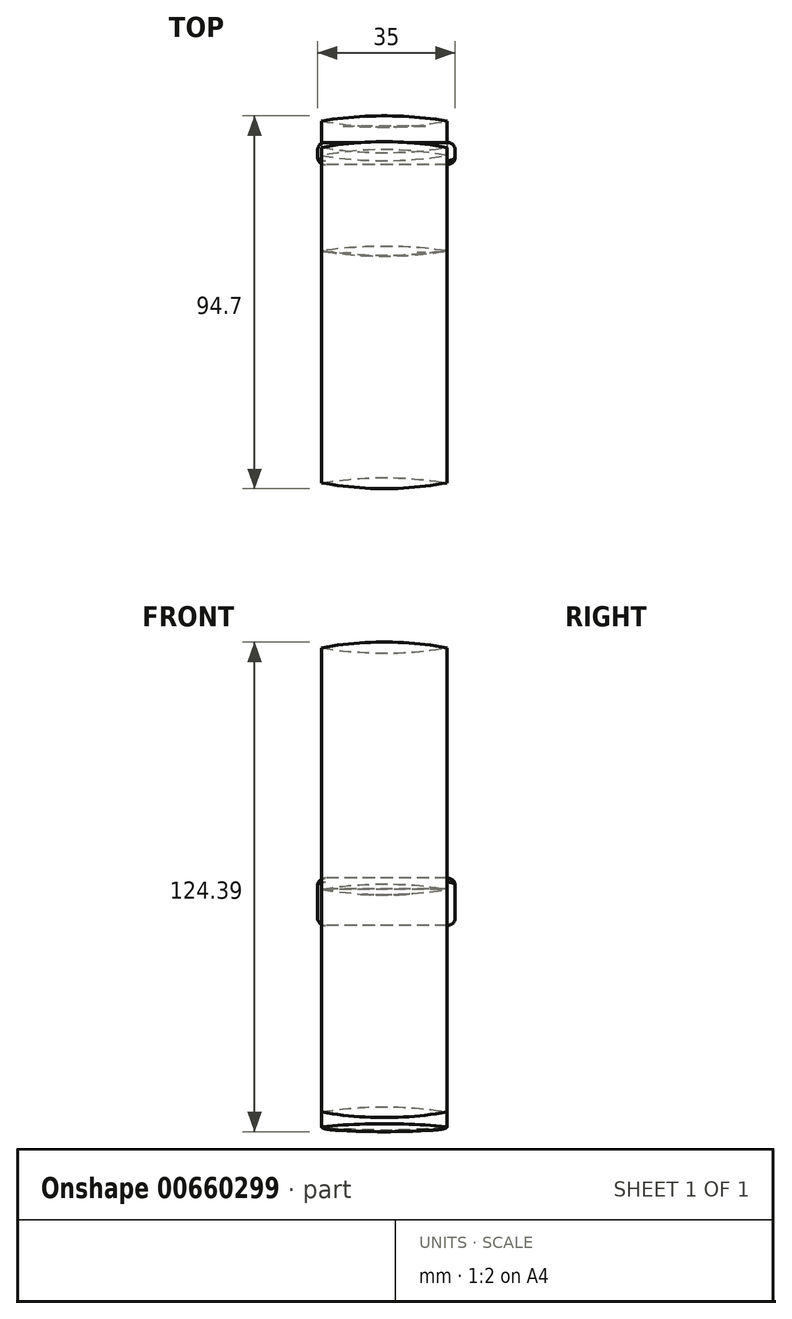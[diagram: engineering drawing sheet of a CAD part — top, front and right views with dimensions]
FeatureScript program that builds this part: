
annotation { "Feature Type Name" : "Feature", "Feature Type Description" : "" }
export const myFeature = defineFeature(function(context is Context, id is Id, definition is map)
    precondition{}
    {
        {
            var Q0;
            Q0=qCreatedBy(makeId("Top.planeOp"),FACE);
            var sketch = newSketch(context, id + "F0", { "sketchPlane" : qUnion([Q0])});
            skArc(sketch, "E0", {"start": v(-16.47, 0) * mm, "mid": v(-0.55, -1.33) * mm, "end": v(15.38, 0) * mm});
            skArc(sketch, "E1", {"start": v(15.38, 0) * mm, "mid": v(-0.55, 1.47) * mm, "end": v(-16.47, 0) * mm});
            skSolve(sketch);
        }
        {
            var Q0;
            Q0=qCreatedBy(makeId("Right.planeOp"),FACE);
            var sketch = newSketch(context, id + "F1", { "sketchPlane" : qUnion([Q0])});
            skFitSpline(sketch, "E2", {"points": [v(0, 0) * mm, v(-1.85, 40.13) * mm, v(-35.62, 61.32) * mm, v(-75.95, 34.52) * mm, v(-76.22, -31.24) * mm, v(-41.63, -54.76) * mm, v(7.26, 0) * mm, v(3.84, -24.36) * mm, v(-24.78, -61.25) * mm], "startDerivative": vector(52.1, 364.79) * mm, "endDerivative": vector(-356.68, -458.43) * mm});
            skSolve(sketch);
        }
        {
            var Q0;
            Q0=makeQuery(id+"F0.imprint","IMPRINT",FACE,{"disambiguationData":[TD([[makeQuery(id+"F0.imprint","IMPRINT",EDGE,{"derivedFrom":sQuery(id+"F0.wireOp",EDGE,"E0")}),1.0]])]});
            var Q1;
            Q1=sQuery(id+"F1.wireOp",EDGE,"E2");
            sweep(context, id + "F2", {"profiles" : qUnion([Q0]), "path" : qUnion([Q1])});
        }
        {
            var Q0;
            Q0=makeQuery(id+"F2.opSweep","CAP_EDGE",EDGE,{"disambiguationData":[OSD([sQuery(id+"F0.wireOp",EDGE,"E1"),sQuery(id+"F1.wireOp",VERTEX,"E2.end")])],"isStart":false});
            var Q1;
            Q1=makeQuery(id+"F2.opSweep","CAP_EDGE",EDGE,{"disambiguationData":[OSD([sQuery(id+"F0.wireOp",EDGE,"E0"),sQuery(id+"F1.wireOp",VERTEX,"E2.end")])],"isStart":false});
            fillet(context, id + "F3", {"entities" : qUnion([Q0, Q1]), "radius" : 1 * mm, "tangentPropagation" : true, "allowEdgeOverflow" : false});
        }
        {
            var Q0;
            Q0=qCreatedBy(makeId("Right.planeOp"),FACE);
            var sketch = newSketch(context, id + "F4", { "sketchPlane" : qUnion([Q0])});
            skLineSegment(sketch, "E3.bottom", {"start": v(3.3, 2.8) * mm, "end": v(-2.3, 2.8) * mm});
            skLineSegment(sketch, "E3.top", {"start": v(3.3, -9.23) * mm, "end": v(-2.3, -9.23) * mm});
            skLineSegment(sketch, "E3.left", {"start": v(3.3, 2.8) * mm, "end": v(3.3, -9.23) * mm});
            skLineSegment(sketch, "E3.right", {"start": v(-2.3, 2.8) * mm, "end": v(-2.3, -9.23) * mm});
            skSolve(sketch);
        }
        {
            var Q0;
            Q0 = qSketchRegion(id + "F4", true);
            extrude(context, id + "F5", {"entities" : qUnion([Q0]), "endBound" : BoundingType.SYMMETRIC, "depth" : 35 * mm, "offsetDistance" : 25 * mm});
        }
        {
            var Q0;
            Q0=makeQuery(id+"F5.opExtrude","SWEPT_EDGE",EDGE,{"disambiguationData":[OSD([sQuery(id+"F4.wireOp",EDGE,"E3.top"),sQuery(id+"F4.wireOp",EDGE,"E3.left")])]});
            var Q1;
            Q1=makeQuery(id+"F5.opExtrude","CAP_EDGE",EDGE,{"disambiguationData":[OSD([sQuery(id+"F4.wireOp",EDGE,"E3.left")])],"isStart":true});
            var Q2;
            Q2=makeQuery(id+"F5.opExtrude","CAP_EDGE",EDGE,{"disambiguationData":[OSD([sQuery(id+"F4.wireOp",EDGE,"E3.right")])],"isStart":true});
            var Q3;
            Q3=makeQuery(id+"F5.opExtrude","SWEPT_EDGE",EDGE,{"disambiguationData":[OSD([sQuery(id+"F4.wireOp",EDGE,"E3.top"),sQuery(id+"F4.wireOp",EDGE,"E3.right")])]});
            var Q4;
            Q4=makeQuery(id+"F5.opExtrude","SWEPT_EDGE",EDGE,{"disambiguationData":[OSD([sQuery(id+"F4.wireOp",EDGE,"E3.bottom"),sQuery(id+"F4.wireOp",EDGE,"E3.left")])]});
            var Q5;
            Q5=makeQuery(id+"F5.opExtrude","CAP_EDGE",EDGE,{"disambiguationData":[OSD([sQuery(id+"F4.wireOp",EDGE,"E3.bottom")])],"isStart":true});
            var Q6;
            Q6=makeQuery(id+"F5.opExtrude","CAP_EDGE",EDGE,{"disambiguationData":[OSD([sQuery(id+"F4.wireOp",EDGE,"E3.top")])],"isStart":true});
            var Q7;
            Q7=makeQuery(id+"F5.opExtrude","CAP_EDGE",EDGE,{"disambiguationData":[OSD([sQuery(id+"F4.wireOp",EDGE,"E3.left")])],"isStart":false});
            var Q8;
            Q8=makeQuery(id+"F5.opExtrude","CAP_EDGE",EDGE,{"disambiguationData":[OSD([sQuery(id+"F4.wireOp",EDGE,"E3.right")])],"isStart":false});
            var Q9;
            Q9=makeQuery(id+"F5.opExtrude","CAP_EDGE",EDGE,{"disambiguationData":[OSD([sQuery(id+"F4.wireOp",EDGE,"E3.bottom")])],"isStart":false});
            var Q10;
            Q10=makeQuery(id+"F5.opExtrude","CAP_EDGE",EDGE,{"disambiguationData":[OSD([sQuery(id+"F4.wireOp",EDGE,"E3.top")])],"isStart":false});
            fillet(context, id + "F6", {"entities" : qUnion([Q0, Q1, Q2, Q3, Q4, Q5, Q6, Q7, Q8, Q9, Q10]), "radius" : 2 * mm, "tangentPropagation" : true, "allowEdgeOverflow" : false});
        }
        {
            var Q0;
            Q0=makeQuery(id+"F5.opExtrude","SWEPT_EDGE",EDGE,{"disambiguationData":[OSD([sQuery(id+"F4.wireOp",EDGE,"E3.bottom"),sQuery(id+"F4.wireOp",EDGE,"E3.right")])]});
            fillet(context, id + "F7", {"entities" : qUnion([Q0]), "radius" : 1 * mm, "tangentPropagation" : true, "allowEdgeOverflow" : false});
        }
    });
